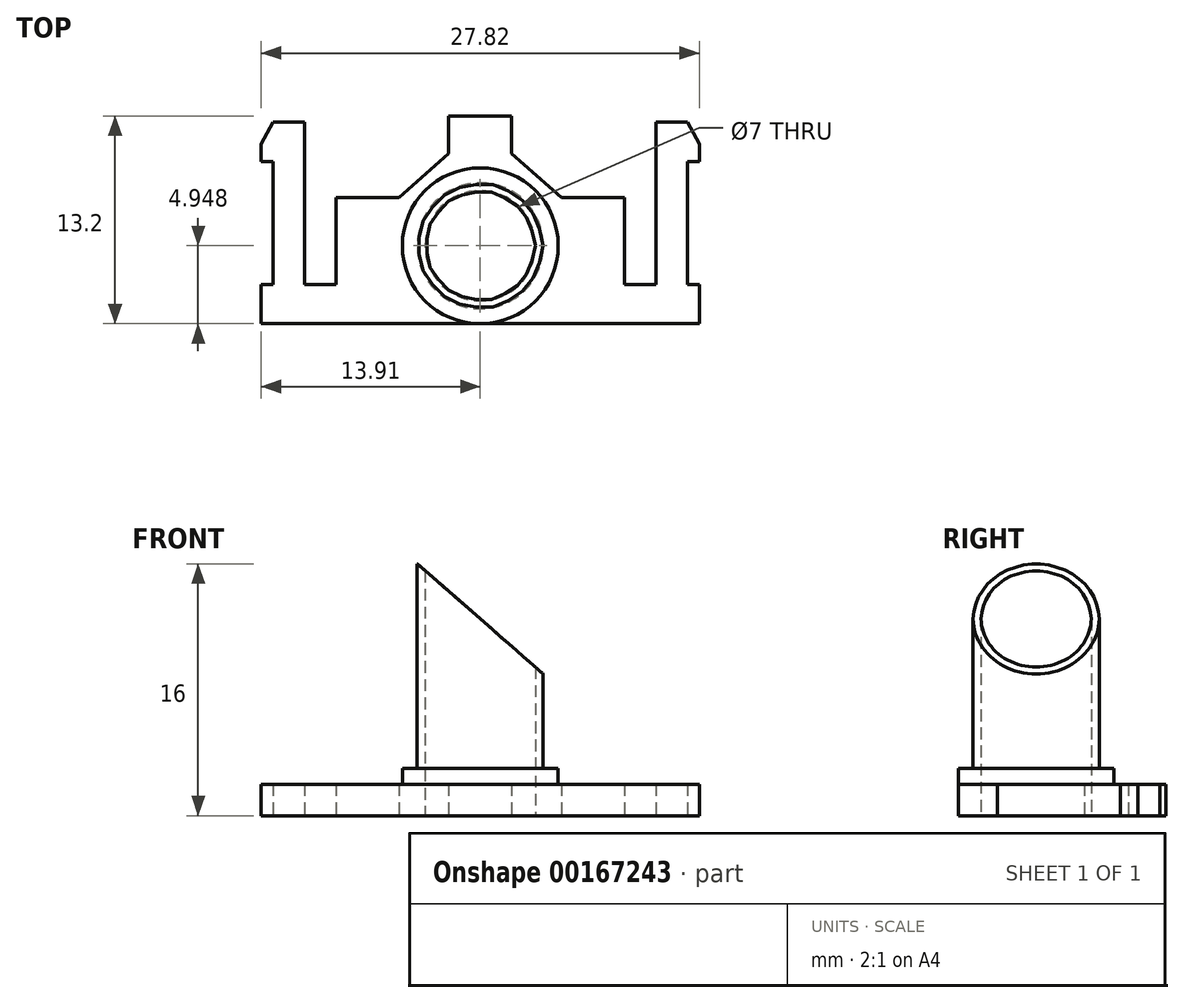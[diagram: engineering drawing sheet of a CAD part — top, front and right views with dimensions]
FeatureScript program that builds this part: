
annotation { "Feature Type Name" : "Feature", "Feature Type Description" : "" }
export const myFeature = defineFeature(function(context is Context, id is Id, definition is map)
    precondition{}
    {
        {
            var Q0;
            Q0=qCreatedBy(makeId("Top.planeOp"),FACE);
            var sketch = newSketch(context, id + "F0", { "sketchPlane" : qUnion([Q0])});
            skLineSegment(sketch, "E0", {"start": v(0, -1.7) * mm, "end": v(13.9, -1.7) * mm});
            skLineSegment(sketch, "E1", {"start": v(13.9, -1.7) * mm, "end": v(13.9, 0.8) * mm});
            skLineSegment(sketch, "E2", {"start": v(13.9, 0.8) * mm, "end": v(13.16, 0.8) * mm});
            skLineSegment(sketch, "E3", {"start": v(13.16, 0.8) * mm, "end": v(13.16, 8.6) * mm});
            skLineSegment(sketch, "E4", {"start": v(13.16, 8.6) * mm, "end": v(13.9, 8.6) * mm});
            skLineSegment(sketch, "E5", {"start": v(13.9, 8.6) * mm, "end": v(13.9, 9.7) * mm});
            skLineSegment(sketch, "E6", {"start": v(13.9, 9.7) * mm, "end": v(13.16, 11.1) * mm});
            skLineSegment(sketch, "E7", {"start": v(13.16, 11.1) * mm, "end": v(11.16, 11.1) * mm});
            skLineSegment(sketch, "E8", {"start": v(11.16, 11.1) * mm, "end": v(11.16, 0.8) * mm});
            skLineSegment(sketch, "E9", {"start": v(11.16, 0.8) * mm, "end": v(9.16, 0.8) * mm});
            skLineSegment(sketch, "E10", {"start": v(9.16, 0.8) * mm, "end": v(9.16, 6.3) * mm});
            skLineSegment(sketch, "E11", {"start": v(9.16, 6.3) * mm, "end": v(5.16, 6.3) * mm});
            skLineSegment(sketch, "E12", {"start": v(5.16, 6.3) * mm, "end": v(2, 9.11) * mm});
            skLineSegment(sketch, "E13", {"start": v(2, 9.11) * mm, "end": v(2, 11.5) * mm});
            skLineSegment(sketch, "E14", {"start": v(2, 11.5) * mm, "end": v(0, 11.5) * mm});
            skCircle(sketch, "E15", {"center": v(0, 3.26) * mm, "radius": 4.95 * mm});
            skCircle(sketch, "E16", {"center": v(0, 3.26) * mm, "radius": 4 * mm});
            skCircle(sketch, "E17", {"center": v(0, 3.26) * mm, "radius": 3.5 * mm});
            skLineSegment(sketch, "E18.MirrorCS", {"start": v(-2, 11.5) * mm, "end": v(0, 11.5) * mm});
            skLineSegment(sketch, "E19.MirrorCS", {"start": v(-2, 9.11) * mm, "end": v(-2, 11.5) * mm});
            skLineSegment(sketch, "E20.MirrorCS", {"start": v(-5.16, 6.3) * mm, "end": v(-2, 9.11) * mm});
            skLineSegment(sketch, "E21.MirrorCS", {"start": v(-9.16, 6.3) * mm, "end": v(-5.16, 6.3) * mm});
            skLineSegment(sketch, "E22.MirrorCS", {"start": v(-9.16, 0.8) * mm, "end": v(-9.16, 6.3) * mm});
            skLineSegment(sketch, "E23.MirrorCS", {"start": v(-11.16, 0.8) * mm, "end": v(-9.16, 0.8) * mm});
            skLineSegment(sketch, "E24.MirrorCS", {"start": v(-11.16, 11.1) * mm, "end": v(-11.16, 0.8) * mm});
            skLineSegment(sketch, "E25.MirrorCS", {"start": v(-13.16, 11.1) * mm, "end": v(-11.16, 11.1) * mm});
            skLineSegment(sketch, "E26.MirrorCS", {"start": v(-13.9, 9.7) * mm, "end": v(-13.16, 11.1) * mm});
            skLineSegment(sketch, "E27.MirrorCS", {"start": v(-13.9, 8.6) * mm, "end": v(-13.9, 9.7) * mm});
            skLineSegment(sketch, "E28.MirrorCS", {"start": v(-13.16, 8.6) * mm, "end": v(-13.9, 8.6) * mm});
            skLineSegment(sketch, "E29.MirrorCS", {"start": v(-13.16, 0.8) * mm, "end": v(-13.16, 8.6) * mm});
            skLineSegment(sketch, "E30.MirrorCS", {"start": v(-13.9, 0.8) * mm, "end": v(-13.16, 0.8) * mm});
            skLineSegment(sketch, "E31.MirrorCS", {"start": v(-13.9, -1.7) * mm, "end": v(-13.9, 0.8) * mm});
            skLineSegment(sketch, "E32.MirrorCS", {"start": v(0, -1.7) * mm, "end": v(-13.9, -1.7) * mm});
            skSolve(sketch);
        }
        {
            var Q0;
            Q0 = qSketchRegion(id + "F0", true);
            extrude(context, id + "F1", {"entities" : qUnion([Q0]), "depth" : 2 * mm});
        }
        {
            var Q0;
            Q0=makeQuery(id+"F0.imprint","IMPRINT",FACE,{"disambiguationData":[TD([[makeQuery(id+"F0.imprint","IMPRINT",EDGE,{"derivedFrom":sQuery(id+"F0.wireOp",EDGE,"E15")}),1.0]])]});
            extrude(context, id + "F2", {"entities" : qUnion([Q0]), "operationType" : NewBodyOperationType.ADD, "depth" : 3 * mm});
        }
        {
            var Q0;
            Q0=makeQuery(id+"F0.imprint","IMPRINT",FACE,{"disambiguationData":[TD([[makeQuery(id+"F0.imprint","IMPRINT",EDGE,{"derivedFrom":sQuery(id+"F0.wireOp",EDGE,"E16")}),1.0]])]});
            extrude(context, id + "F3", {"entities" : qUnion([Q0]), "operationType" : NewBodyOperationType.ADD, "depth" : 16 * mm});
        }
        {
            var Q0;
            Q0=qCreatedBy(makeId("Front.planeOp"),FACE);
            var sketch = newSketch(context, id + "F4", { "sketchPlane" : qUnion([Q0])});
            skLineSegment(sketch, "E33.0", {"start": v(-4, 16) * mm, "end": v(4, 16) * mm});
            skLineSegment(sketch, "E34", {"start": v(4, 16) * mm, "end": v(4, 9) * mm});
            skLineSegment(sketch, "E35", {"start": v(4, 9) * mm, "end": v(-4, 16) * mm});
            skSolve(sketch);
        }
        {
            var Q0;
            Q0 = qSketchRegion(id + "F4", true);
            extrude(context, id + "F5", {"entities" : qUnion([Q0]), "operationType" : NewBodyOperationType.REMOVE, "endBound" : BoundingType.SYMMETRIC, "oppositeDirection" : true, "depth" : 18.8 * mm});
        }
    });
